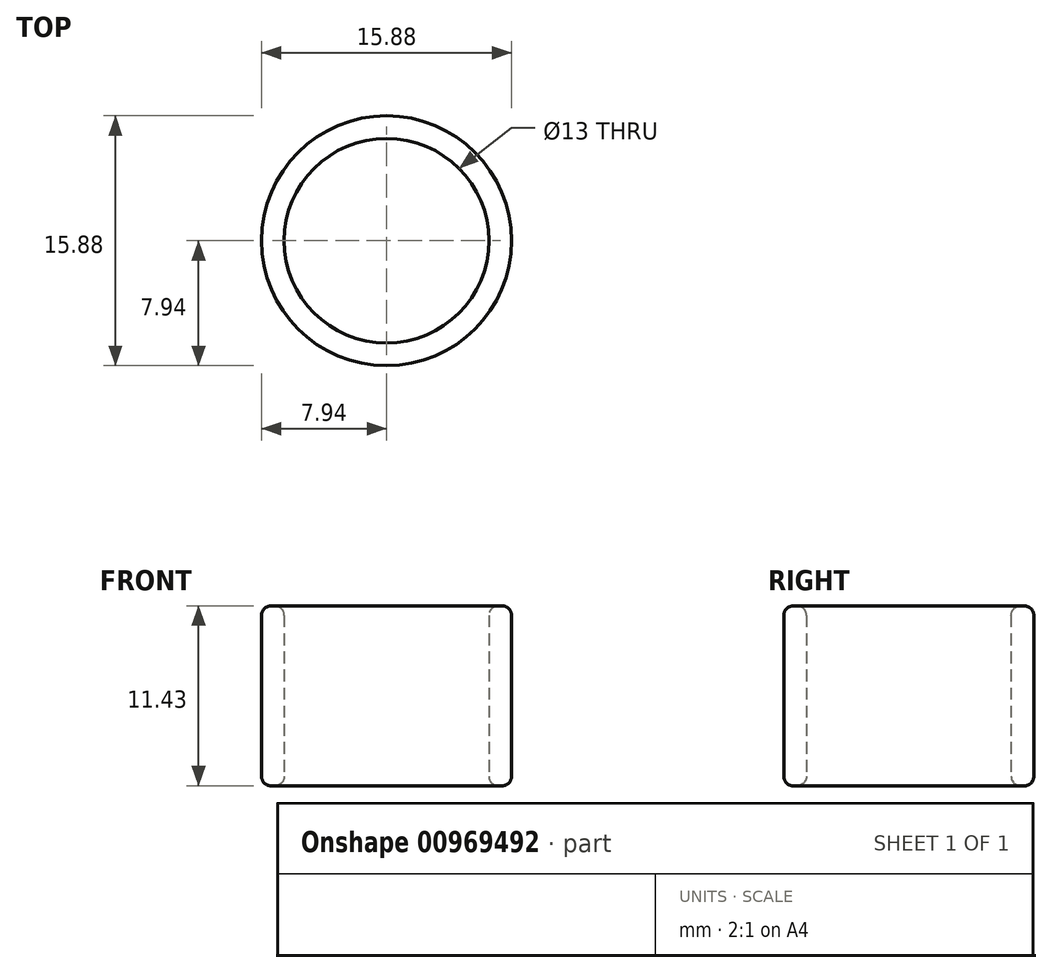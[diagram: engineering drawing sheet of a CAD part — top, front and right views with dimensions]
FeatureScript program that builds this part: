
annotation { "Feature Type Name" : "Feature", "Feature Type Description" : "" }
export const myFeature = defineFeature(function(context is Context, id is Id, definition is map)
    precondition{}
    {
        {
            var Q0;
            Q0=qCreatedBy(makeId("Top.planeOp"),FACE);
            var sketch = newSketch(context, id + "F0", { "sketchPlane" : qUnion([Q0])});
            skCircle(sketch, "E0", {"center": v(0, 0) * mm, "radius": 6.5 * mm});
            skCircle(sketch, "E1", {"center": v(0, 0) * mm, "radius": 7.94 * mm});
            skSolve(sketch);
        }
        {
            var Q0;
            Q0=qSketchRegion(id+"F0",true);
            extrude(context, id + "F1", {"entities" : qUnion([Q0]), "depth" : 11.43 * mm, "offsetDistance" : 25 * mm});
        }
        {
            var Q0;
            Q0=makeQuery(id+"F1.opExtrude","CAP_EDGE",EDGE,{"disambiguationData":[OSD([sQuery(id+"F0.wireOp",EDGE,"E0")])],"isStart":true});
            var Q1;
            Q1=makeQuery(id+"F1.opExtrude","CAP_EDGE",EDGE,{"disambiguationData":[OSD([sQuery(id+"F0.wireOp",EDGE,"E1")])],"isStart":false});
            var Q2;
            Q2=makeQuery(id+"F1.opExtrude","CAP_EDGE",EDGE,{"disambiguationData":[OSD([sQuery(id+"F0.wireOp",EDGE,"E0")])],"isStart":false});
            fillet(context, id + "F2", {"entities" : qUnion([Q0, Q1, Q2]), "radius" : .6 * mm, "tangentPropagation" : true, "allowEdgeOverflow" : false});
        }
        {
            var Q0;
            Q0=makeQuery(id+"F1.opExtrude","CAP_EDGE",EDGE,{"disambiguationData":[OSD([sQuery(id+"F0.wireOp",EDGE,"E1")])],"isStart":true});
            fillet(context, id + "F3", {"entities" : qUnion([Q0]), "radius" : .6 * mm, "allowEdgeOverflow" : false});
        }
    });
